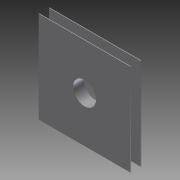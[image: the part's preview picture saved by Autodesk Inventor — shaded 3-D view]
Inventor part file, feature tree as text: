
AUTODESK INVENTOR PART (.ipt)
format: ipt  version: 2011 (Build 150239000, 239)  size: 114,176 bytes
history: native  units: in
note: dims shown in document units (in); Inventor stores cm internally (conversion verified against a paired STEP export)
features: extrude x6, sketch x6
ambient origin geometry x8: Origin, YZ Plane, XZ Plane, XY Plane, X Axis, Y Axis, Z Axis, Center Point
bodies: Solid1 (feature_tree)
feature tree (12):
  extrude  "Extrusion1"  Depth=4.0in
  extrude  "Extrusion2"  Depth=0.32in TaperAngle=0.0deg
  extrude  "Extrusion3"  Depth=0.32in TaperAngle=0.0deg
  extrude  "Extrusion4"  Depth=0.03in
  extrude  "Extrusion5"  Depth=1.5in
  extrude  "Extrusion6"  Depth=1.0in TaperAngle=0.0deg
  sketch  "Sketch1"  dims[d0=4.0in d1=4.0in]
  sketch  "Sketch2"  dims[d2=1.0in d3=0.32in d4=0.155in d5=0.0in d6=0.0in]
  sketch  "Sketch3"  dims[d7=1.0in d8=0.32in d9=0.0in]
  sketch  "Sketch4"  dims[d10=0.03in d11=0.03in]
  sketch  "Sketch5"  dims[d12=4.0in d13=0.0in d14=1.5in]
  sketch  "Sketch6"  dims[d15=0.32in d16=0.0in d17=1.0in d18=0.0in d19=0.14in d20=0.0in]
